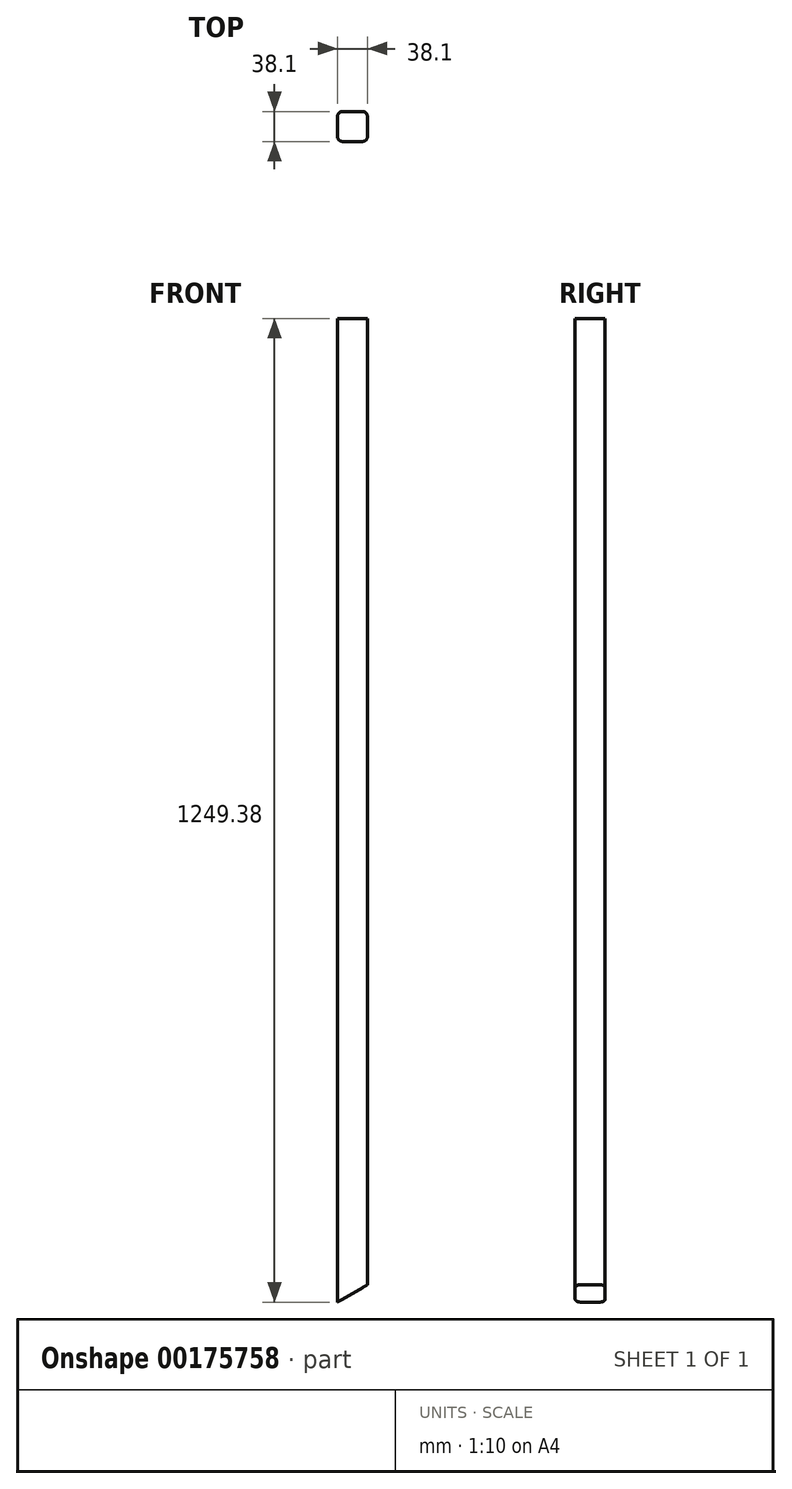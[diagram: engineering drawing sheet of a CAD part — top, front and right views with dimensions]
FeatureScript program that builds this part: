
annotation { "Feature Type Name" : "Feature", "Feature Type Description" : "" }
export const myFeature = defineFeature(function(context is Context, id is Id, definition is map)
    precondition{}
    {
        {
            var Q0;
            Q0=qCreatedBy(makeId("Top.planeOp"),FACE);
            var sketch = newSketch(context, id + "F0", { "sketchPlane" : qUnion([Q0])});
            skLineSegment(sketch, "E0.bottom", {"start": v(12.7, 19.05) * mm, "end": v(-12.7, 19.05) * mm});
            skLineSegment(sketch, "E0.top", {"start": v(12.7, -19.05) * mm, "end": v(-12.7, -19.05) * mm});
            skLineSegment(sketch, "E0.left", {"start": v(19.05, 12.7) * mm, "end": v(19.05, -12.7) * mm});
            skLineSegment(sketch, "E0.right", {"start": v(-19.05, 12.7) * mm, "end": v(-19.05, -12.7) * mm});
            skPoint(sketch, "E0.middle", {"position": v(0, 0) * mm});
            skPoint(sketch, "E1.visualSharp", {"position": v(-19.05, 19.05) * mm});
            skArc(sketch, "E1.filletArc", {"start": v(-12.7, 19.05) * mm, "mid": v(-17.2, 17.2) * mm, "end": v(-19.05, 12.7) * mm});
            skPoint(sketch, "E2.visualSharp", {"position": v(19.05, 19.05) * mm});
            skArc(sketch, "E2.filletArc", {"start": v(19.05, 12.7) * mm, "mid": v(17.2, 17.2) * mm, "end": v(12.7, 19.05) * mm});
            skPoint(sketch, "E3.visualSharp", {"position": v(19.05, -19.05) * mm});
            skArc(sketch, "E3.filletArc", {"start": v(12.7, -19.05) * mm, "mid": v(17.2, -17.2) * mm, "end": v(19.05, -12.7) * mm});
            skPoint(sketch, "E4.visualSharp", {"position": v(-19.05, -19.05) * mm});
            skArc(sketch, "E4.filletArc", {"start": v(-19.05, -12.7) * mm, "mid": v(-17.2, -17.2) * mm, "end": v(-12.7, -19.05) * mm});
            skSolve(sketch);
        }
        {
            var Q0;
            Q0=qSketchRegion(id+"F0",true);
            extrude(context, id + "F1", {"entities" : qUnion([Q0]), "depth" : 1249.68 * mm, "offsetDistance" : 25.4 * mm});
        }
        {
            var Q0;
            Q0=qCreatedBy(makeId("Front.planeOp"),FACE);
            var sketch = newSketch(context, id + "F2", { "sketchPlane" : qUnion([Q0])});
            skLineSegment(sketch, "E5", {"start": v(-19.57, 0) * mm, "end": v(19.05, 22.3) * mm});
            skLineSegment(sketch, "E6", {"start": v(19.05, 22.3) * mm, "end": v(19.05, 0) * mm});
            skLineSegment(sketch, "E7", {"start": v(19.05, 0) * mm, "end": v(-19.57, 0) * mm});
            skSolve(sketch);
        }
        {
            var Q0;
            Q0 = qSketchRegion(id + "F2", true);
            extrude(context, id + "F3", {"entities" : qUnion([Q0]), "operationType" : NewBodyOperationType.REMOVE, "endBound" : BoundingType.SYMMETRIC, "depth" : 38.1 * mm, "offsetDistance" : 25.4 * mm});
        }
    });
